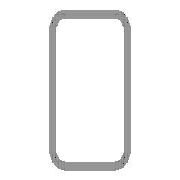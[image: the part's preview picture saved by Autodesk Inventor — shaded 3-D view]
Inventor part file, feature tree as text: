
AUTODESK INVENTOR PART (.ipt)
format: ipt  version: 2025.1 (Build 291241020, 241B)  size: 135,168 bytes
history: native  units: mm (DEFAULTED — no unit token found)
features: other x4, sketch x1, plane x1
ambient origin geometry x8: Origin, YZ Plane, XZ Plane, XY Plane, X Axis, Y Axis, Z Axis, Center Point
bodies: Solid1 (feature_tree), Body (feature_tree)
feature tree (6):
  parser-record x1  (decoder bookkeeping rows leaked as tree rows — omitted from the tree; the rows remain in map.json)
  other  "Driven Length"
  other  "Start Plane"
  other  "End Plane"
  sketch  "Sketch3"  dims[d3=620.0mm d4=0.0mm d7=4.0mm d9=20.0mm d11=40.0mm d12=2.0mm d13=-0.0mm d14=620.0mm d15=10.0mm d16=20.0mm d17=90.0deg d18=620.0mm]
  plane  "Work Plane3"
